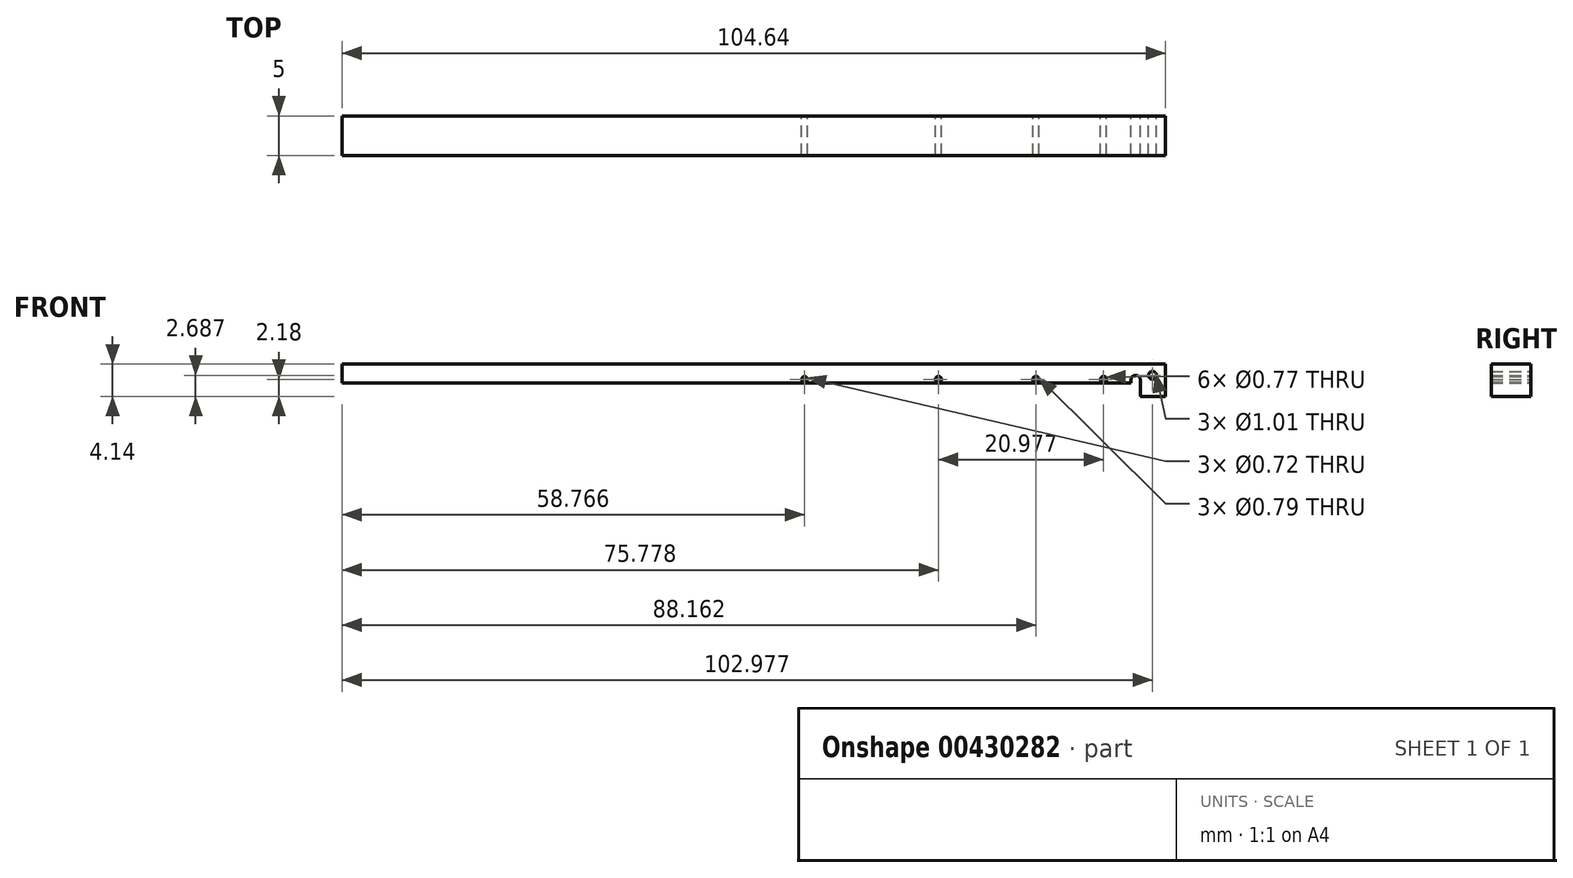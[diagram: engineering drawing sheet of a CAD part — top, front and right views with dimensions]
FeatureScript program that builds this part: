
annotation { "Feature Type Name" : "Feature", "Feature Type Description" : "" }
export const myFeature = defineFeature(function(context is Context, id is Id, definition is map)
    precondition{}
    {
        {
            var Q0;
            Q0=qCreatedBy(makeId("Front.planeOp"),FACE);
            var sketch = newSketch(context, id + "F0", { "sketchPlane" : qUnion([Q0])});
            skLineSegment(sketch, "E0", {"start": v(-48.22, 0) * mm, "end": v(52, 0) * mm});
            skLineSegment(sketch, "E1", {"start": v(52, 0) * mm, "end": v(52, 0.36) * mm});
            skArc(sketch, "E2", {"start": v(52, 0.36) * mm, "mid": v(52.6, 0.96) * mm, "end": v(53.2, 0.36) * mm});
            skLineSegment(sketch, "E3", {"start": v(53.2, 0.36) * mm, "end": v(53.2, -1.73) * mm});
            skLineSegment(sketch, "E4", {"start": v(53.2, -1.73) * mm, "end": v(56.42, -1.73) * mm});
            skLineSegment(sketch, "E5", {"start": v(56.42, -1.73) * mm, "end": v(56.42, 2.41) * mm});
            skLineSegment(sketch, "E6", {"start": v(56.42, 2.41) * mm, "end": v(-48.2, 2.41) * mm});
            skLineSegment(sketch, "E7", {"start": v(-48.2, 2.41) * mm, "end": v(-48.22, 0) * mm});
            skPoint(sketch, "E8", {"position": v(54.76, 0.96) * mm});
            skCircle(sketch, "E9", {"center": v(54.76, 0.96) * mm, "radius": 0.5 * mm});
            skPoint(sketch, "E10", {"position": v(48.53, 0.45) * mm});
            skPoint(sketch, "E11", {"position": v(39.94, 0.45) * mm});
            skPoint(sketch, "E12", {"position": v(27.56, 0.45) * mm});
            skPoint(sketch, "E13", {"position": v(10.55, 0.45) * mm});
            skCircle(sketch, "E14", {"center": v(10.55, 0.45) * mm, "radius": 0.36 * mm});
            skCircle(sketch, "E15", {"center": v(27.56, 0.45) * mm, "radius": 0.38 * mm});
            skCircle(sketch, "E16", {"center": v(39.94, 0.45) * mm, "radius": 0.4 * mm});
            skCircle(sketch, "E17", {"center": v(48.53, 0.45) * mm, "radius": 0.38 * mm});
            skSolve(sketch);
        }
        {
            var Q0;
            Q0=makeQuery(id+"F0.imprint","IMPRINT",FACE,{"disambiguationData":[TD([[makeQuery(id+"F0.imprint","IMPRINT",EDGE,{"derivedFrom":sQuery(id+"F0.wireOp",EDGE,"E0")}),1.0]])]});
            extrude(context, id + "F1", {"entities" : qUnion([Q0]), "depth" : 5 * mm});
        }
    });
